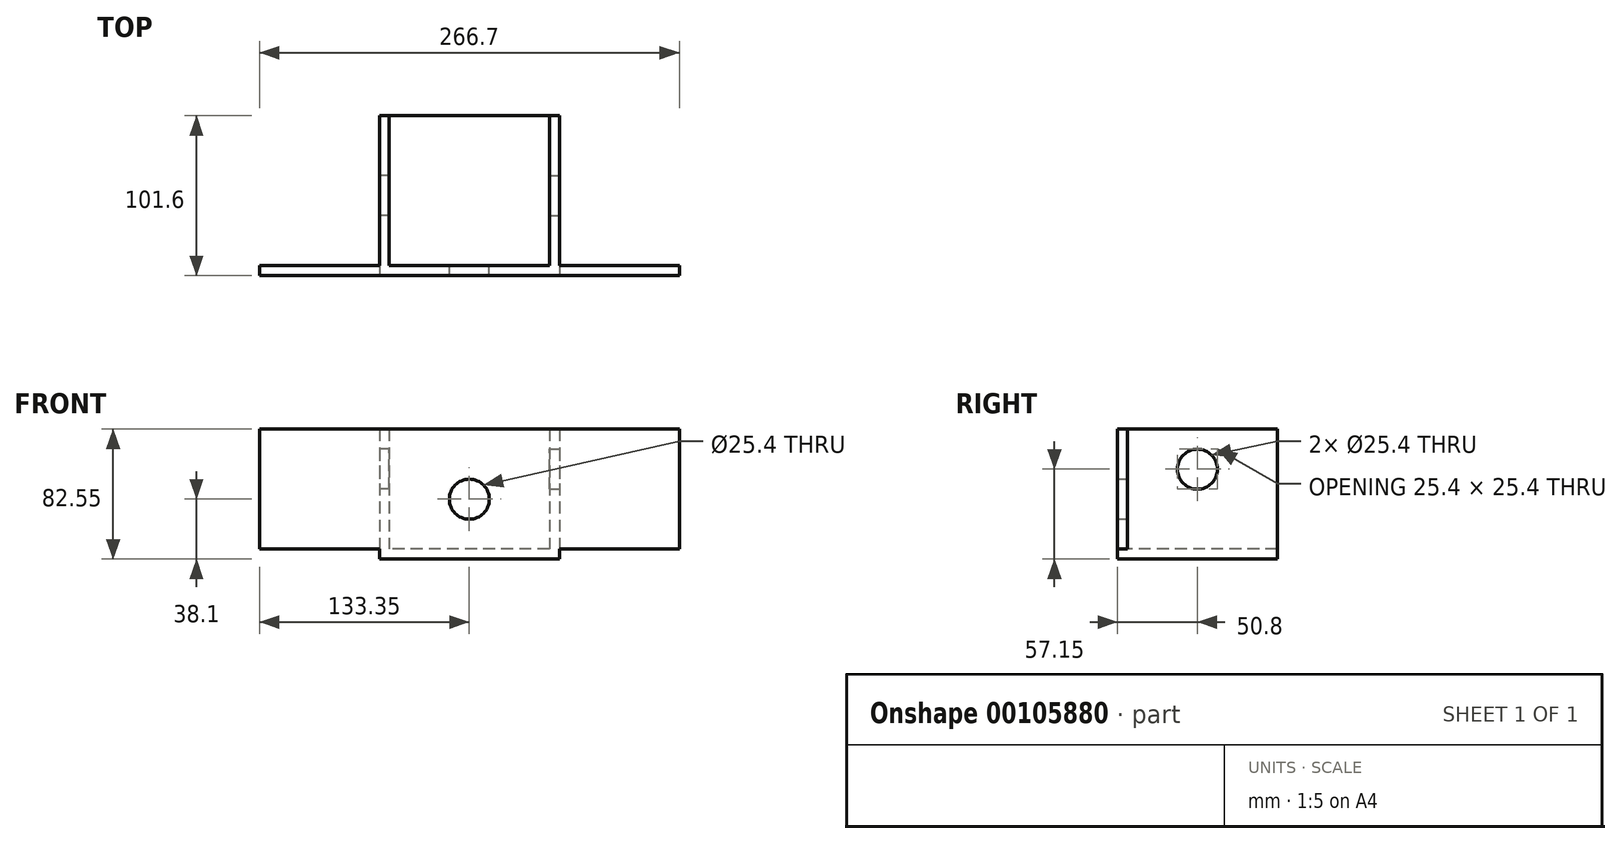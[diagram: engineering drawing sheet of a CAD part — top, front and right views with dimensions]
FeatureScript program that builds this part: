
annotation { "Feature Type Name" : "Feature", "Feature Type Description" : "" }
export const myFeature = defineFeature(function(context is Context, id is Id, definition is map)
    precondition{}
    {
        {
            var Q0;
            Q0=qCreatedBy(makeId("Top.planeOp"),FACE);
            var sketch = newSketch(context, id + "F0", { "sketchPlane" : qUnion([Q0])});
            skLineSegment(sketch, "E0.bottom", {"start": v(0, 50.8) * mm, "end": v(-57.15, 50.8) * mm});
            skLineSegment(sketch, "E0.top", {"start": v(0, -50.8) * mm, "end": v(-57.15, -50.8) * mm});
            skLineSegment(sketch, "E0.right", {"start": v(-57.15, 50.8) * mm, "end": v(-57.15, -50.8) * mm});
            skPoint(sketch, "E0.middle", {"position": v(0, 0) * mm});
            skLineSegment(sketch, "E1", {"start": v(0, 50.8) * mm, "end": v(0, -50.8) * mm});
            skSolve(sketch);
        }
        {
            var Q0;
            Q0 = qSketchRegion(id + "F0", true);
            extrude(context, id + "F1", {"entities" : qUnion([Q0]), "depth" : 6.35 * mm});
        }
        {
            var Q0;
            Q0=makeQuery(id+"F1.opExtrude","CAP_FACE",FACE,{"disambiguationData":[OSD([sQuery(id+"F0.wireOp",EDGE,"E0.bottom"),sQuery(id+"F0.wireOp",EDGE,"E0.top"),sQuery(id+"F0.wireOp",EDGE,"E0.left"),sQuery(id+"F0.wireOp",EDGE,"E0.right")])],"isStart":false});
            var sketch = newSketch(context, id + "F2", { "sketchPlane" : qUnion([Q0])});
            skLineSegment(sketch, "E2.bottom", {"start": v(-57.15, 50.8) * mm, "end": v(-50.8, 50.8) * mm});
            skLineSegment(sketch, "E2.left", {"start": v(-57.15, 50.8) * mm, "end": v(-57.15, -44.45) * mm});
            skLineSegment(sketch, "E2.right", {"start": v(-50.8, 50.8) * mm, "end": v(-50.8, -44.45) * mm});
            skLineSegment(sketch, "E3.bottom", {"start": v(-50.8, -44.45) * mm, "end": v(0, -44.45) * mm});
            skLineSegment(sketch, "E3.right", {"start": v(0, -44.45) * mm, "end": v(0, -50.8) * mm});
            skLineSegment(sketch, "E4.right", {"start": v(-133.35, -50.8) * mm, "end": v(-133.35, -44.45) * mm});
            skLineSegment(sketch, "E5", {"start": v(-133.35, -50.8) * mm, "end": v(0, -50.8) * mm});
            skLineSegment(sketch, "E6", {"start": v(-133.35, -44.45) * mm, "end": v(-57.15, -44.45) * mm});
            skSolve(sketch);
        }
        {
            var Q0;
            Q0 = qSketchRegion(id + "F2", true);
            extrude(context, id + "F3", {"entities" : qUnion([Q0]), "operationType" : NewBodyOperationType.ADD, "depth" : 76.2 * mm});
        }
        {
            var Q0;
            Q0=makeQuery(id+"F3.boolean.opBoolean","MERGE",FACE,{"derivedFrom":[makeQuery(id+"F1.opExtrude","SWEPT_FACE",FACE,{"disambiguationData":[OSD([sQuery(id+"F0.wireOp",EDGE,"E0.right")])]}),makeQuery(id+"F3.opExtrude","SWEPT_FACE",FACE,{"disambiguationData":[OSD([sQuery(id+"F2.wireOp",EDGE,"E2.left")])]})]});
            var sketch = newSketch(context, id + "F4", { "sketchPlane" : qUnion([Q0])});
            skCircle(sketch, "E7", {"center": v(0, 57.15) * mm, "radius": 12.7 * mm});
            skSolve(sketch);
        }
        {
            var Q0;
            Q0 = qSketchRegion(id + "F4", true);
            extrude(context, id + "F5", {"entities" : qUnion([Q0]), "operationType" : NewBodyOperationType.REMOVE, "endBound" : BoundingType.UP_TO_NEXT, "oppositeDirection" : true, "depth" : 25.4 * mm});
        }
        {
            var Q0;
            Q0=makeQuery(id+"F1.opExtrude","SWEPT_BODY",BODY,{"disambiguationData":[OSD([sQuery(id+"F0.wireOp",EDGE,"E0.bottom"),sQuery(id+"F0.wireOp",EDGE,"E0.top"),sQuery(id+"F0.wireOp",EDGE,"E0.right"),sQuery(id+"F0.wireOp",EDGE,"E1")])]});
            var Q1;
            Q1=qCreatedBy(makeId("Right.planeOp"),FACE);
            mirror(context, id + "F6", {"operationType" : NewBodyOperationType.ADD, "entities" : qUnion([Q0]), "mirrorPlane" : qUnion([Q1])});
        }
        {
            var Q0;
            {var subQ0=makeQuery(id+"F3.opExtrude","SWEPT_FACE",FACE,{"disambiguationData":[OSD([sQuery(id+"F2.wireOp",EDGE,"E3.bottom")])]});Q0=makeQuery(id+"F6.boolean.opBoolean","MERGE",FACE,{"derivedFrom":[subQ0,makeQuery(id+"F6.opPattern","COPY",FACE,{"derivedFrom":subQ0,"instanceName":"1"})]});}
            var sketch = newSketch(context, id + "F7", { "sketchPlane" : qUnion([Q0])});
            skCircle(sketch, "E8", {"center": v(0, 38.1) * mm, "radius": 12.7 * mm});
            skSolve(sketch);
        }
        {
            var Q0;
            Q0 = qSketchRegion(id + "F7", true);
            extrude(context, id + "F8", {"entities" : qUnion([Q0]), "operationType" : NewBodyOperationType.REMOVE, "endBound" : BoundingType.UP_TO_NEXT, "oppositeDirection" : true, "depth" : 25.4 * mm});
        }
    });
